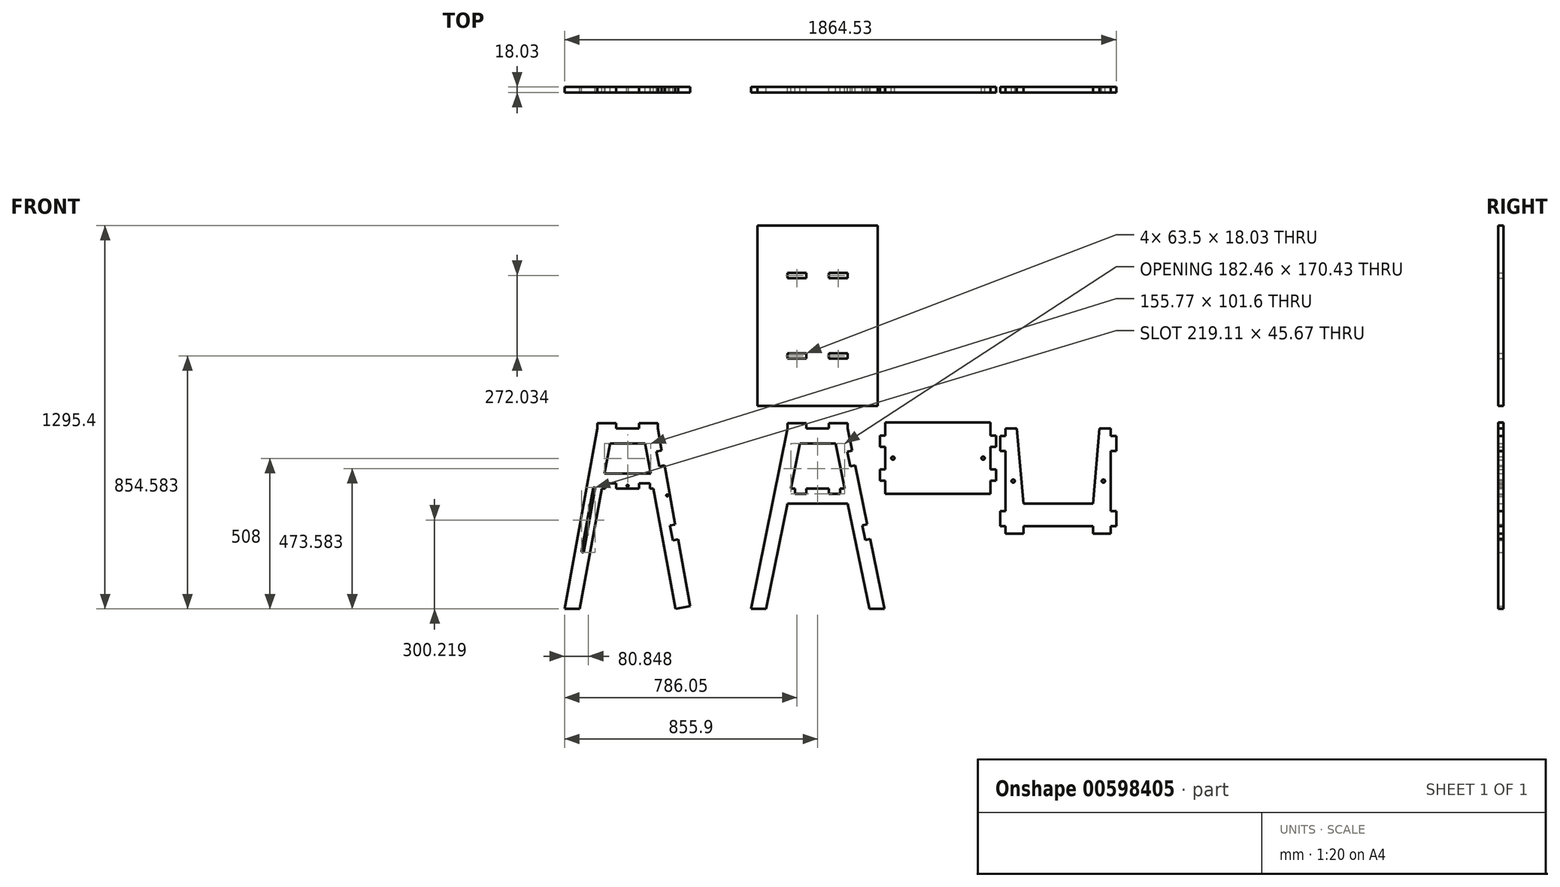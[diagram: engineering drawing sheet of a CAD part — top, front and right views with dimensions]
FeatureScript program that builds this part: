
annotation { "Feature Type Name" : "Feature", "Feature Type Description" : "" }
export const myFeature = defineFeature(function(context is Context, id is Id, definition is map)
    precondition{}
    {
        {
            var Q0;
            Q0=qCreatedBy(makeId("Front.planeOp"),FACE);
            var sketch = newSketch(context, id + "F0", { "sketchPlane" : qUnion([Q0])});
            skLineSegment(sketch, "E0", {"start": v(-101.6, 0) * mm, "end": v(101.6, 0) * mm});
            skLineSegment(sketch, "E1", {"start": v(-101.6, 0) * mm, "end": v(-226.03, -609.6) * mm});
            skLineSegment(sketch, "E2", {"start": v(-226.03, -609.6) * mm, "end": v(-174.19, -609.6) * mm});
            skLineSegment(sketch, "E3", {"start": v(-174.19, -609.6) * mm, "end": v(-101.6, -254) * mm});
            skLineSegment(sketch, "E4", {"start": v(-101.6, -254) * mm, "end": v(101.6, -254) * mm});
            skLineSegment(sketch, "E5", {"start": v(0, 0) * mm, "end": v(0, -254) * mm, "construction": true});
            skLineSegment(sketch, "E6.MirrorCS", {"start": v(226.03, -609.6) * mm, "end": v(174.19, -609.6) * mm});
            skLineSegment(sketch, "E7.MirrorCS", {"start": v(174.19, -609.6) * mm, "end": v(101.6, -254) * mm});
            skLineSegment(sketch, "E8.MirrorCS", {"start": v(101.6, 0) * mm, "end": v(226.03, -609.6) * mm});
            skLineSegment(sketch, "E9.0", {"start": v(-60.12, -50.8) * mm, "end": v(60.12, -50.8) * mm});
            skLineSegment(sketch, "E10.0", {"start": v(-91.23, -203.2) * mm, "end": v(91.23, -203.2) * mm});
            skLineSegment(sketch, "E11", {"start": v(-101.6, -254) * mm, "end": v(-60.12, -50.8) * mm, "construction": true});
            skLineSegment(sketch, "E12", {"start": v(-60.12, -50.8) * mm, "end": v(-91.23, -203.2) * mm});
            skLineSegment(sketch, "E13.MirrorCS", {"start": v(60.12, -50.8) * mm, "end": v(91.23, -203.2) * mm});
            skLineSegment(sketch, "E14", {"start": v(-101.6, 0) * mm, "end": v(-101.6, 18.03) * mm});
            skLineSegment(sketch, "E15", {"start": v(-101.6, 18.03) * mm, "end": v(-38.1, 18.03) * mm});
            skLineSegment(sketch, "E16", {"start": v(-38.1, 18.03) * mm, "end": v(-38.1, 0) * mm});
            skLineSegment(sketch, "E17", {"start": v(101.6, 0) * mm, "end": v(101.6, 18.03) * mm});
            skLineSegment(sketch, "E18", {"start": v(101.6, 18.03) * mm, "end": v(38.1, 18.03) * mm});
            skLineSegment(sketch, "E19", {"start": v(38.1, 18.03) * mm, "end": v(38.1, 0) * mm});
            skLineSegment(sketch, "E20", {"start": v(116.84, -74.66) * mm, "end": v(99.17, -78.27) * mm});
            skLineSegment(sketch, "E21", {"start": v(99.17, -78.27) * mm, "end": v(109.33, -128.04) * mm});
            skLineSegment(sketch, "E22", {"start": v(109.33, -128.04) * mm, "end": v(127, -124.43) * mm});
            skLineSegment(sketch, "E23", {"start": v(167.64, -323.53) * mm, "end": v(149.97, -327.14) * mm});
            skLineSegment(sketch, "E24", {"start": v(149.97, -327.14) * mm, "end": v(160.13, -376.9) * mm});
            skLineSegment(sketch, "E25", {"start": v(160.13, -376.9) * mm, "end": v(177.8, -373.3) * mm});
            skLineSegment(sketch, "E26.bottom", {"start": v(-76.2, -203.2) * mm, "end": v(-38.1, -203.2) * mm});
            skLineSegment(sketch, "E26.top", {"start": v(-76.2, -221.23) * mm, "end": v(-38.1, -221.23) * mm});
            skLineSegment(sketch, "E26.left", {"start": v(-76.2, -203.2) * mm, "end": v(-76.2, -221.23) * mm});
            skLineSegment(sketch, "E26.right", {"start": v(-38.1, -203.2) * mm, "end": v(-38.1, -221.23) * mm});
            skLineSegment(sketch, "E27.MirrorCS", {"start": v(76.2, -221.23) * mm, "end": v(38.1, -221.23) * mm});
            skLineSegment(sketch, "E28.MirrorCS", {"start": v(76.2, -203.2) * mm, "end": v(76.2, -221.23) * mm});
            skLineSegment(sketch, "E29.MirrorCS", {"start": v(76.2, -203.2) * mm, "end": v(38.1, -203.2) * mm});
            skLineSegment(sketch, "E30.MirrorCS", {"start": v(38.1, -203.2) * mm, "end": v(38.1, -221.23) * mm});
            skLineSegment(sketch, "E31.bottom", {"start": v(228.6, -221.23) * mm, "end": v(584.2, -221.23) * mm});
            skLineSegment(sketch, "E31.top", {"start": v(228.6, 20.07) * mm, "end": v(584.2, 20.07) * mm});
            skLineSegment(sketch, "E31.left", {"start": v(228.6, -221.23) * mm, "end": v(228.6, 20.07) * mm});
            skLineSegment(sketch, "E31.right", {"start": v(584.2, -221.23) * mm, "end": v(584.2, 20.07) * mm});
            skLineSegment(sketch, "E32", {"start": v(228.6, -100.58) * mm, "end": v(584.2, -100.58) * mm, "construction": true});
            skLineSegment(sketch, "E33.bottom", {"start": v(228.6, -62.48) * mm, "end": v(210.57, -62.48) * mm});
            skLineSegment(sketch, "E33.top", {"start": v(228.6, -24.38) * mm, "end": v(210.57, -24.38) * mm});
            skLineSegment(sketch, "E33.left", {"start": v(228.6, -62.48) * mm, "end": v(228.6, -24.38) * mm});
            skLineSegment(sketch, "E33.right", {"start": v(210.57, -62.48) * mm, "end": v(210.57, -24.38) * mm});
            skLineSegment(sketch, "E34.MirrorCS", {"start": v(210.57, -138.68) * mm, "end": v(210.57, -176.78) * mm});
            skLineSegment(sketch, "E35.MirrorCS", {"start": v(228.6, -176.78) * mm, "end": v(210.57, -176.78) * mm});
            skLineSegment(sketch, "E36.MirrorCS", {"start": v(228.6, -138.68) * mm, "end": v(228.6, -176.78) * mm});
            skLineSegment(sketch, "E37.MirrorCS", {"start": v(228.6, -138.68) * mm, "end": v(210.57, -138.68) * mm});
            skLineSegment(sketch, "E38", {"start": v(406.4, 20.07) * mm, "end": v(406.4, -221.23) * mm, "construction": true});
            skLineSegment(sketch, "E39.MirrorCS", {"start": v(602.23, -62.48) * mm, "end": v(602.23, -24.38) * mm});
            skLineSegment(sketch, "E40.MirrorCS", {"start": v(584.2, -138.68) * mm, "end": v(602.23, -138.68) * mm});
            skLineSegment(sketch, "E41.MirrorCS", {"start": v(584.2, -62.48) * mm, "end": v(584.2, -24.38) * mm});
            skLineSegment(sketch, "E42.MirrorCS", {"start": v(584.2, -176.78) * mm, "end": v(602.23, -176.78) * mm});
            skLineSegment(sketch, "E43.MirrorCS", {"start": v(584.2, -24.38) * mm, "end": v(602.23, -24.38) * mm});
            skLineSegment(sketch, "E44.MirrorCS", {"start": v(602.23, -138.68) * mm, "end": v(602.23, -176.78) * mm});
            skLineSegment(sketch, "E45.MirrorCS", {"start": v(584.2, -62.48) * mm, "end": v(602.23, -62.48) * mm});
            skLineSegment(sketch, "E46.MirrorCS", {"start": v(584.2, -138.68) * mm, "end": v(584.2, -176.78) * mm});
            skLineSegment(sketch, "E47", {"start": v(635, 0) * mm, "end": v(635, -355.6) * mm});
            skLineSegment(sketch, "E48.bottom", {"start": v(635, -25.4) * mm, "end": v(616.97, -25.4) * mm});
            skLineSegment(sketch, "E48.top", {"start": v(635, -76.2) * mm, "end": v(616.97, -76.2) * mm});
            skLineSegment(sketch, "E48.left", {"start": v(635, -25.4) * mm, "end": v(635, -76.2) * mm});
            skLineSegment(sketch, "E48.right", {"start": v(616.97, -25.4) * mm, "end": v(616.97, -76.2) * mm});
            skLineSegment(sketch, "E49.bottom", {"start": v(635, -330.2) * mm, "end": v(616.97, -330.2) * mm});
            skLineSegment(sketch, "E49.top", {"start": v(635, -279.4) * mm, "end": v(616.97, -279.4) * mm});
            skLineSegment(sketch, "E49.left", {"start": v(635, -330.2) * mm, "end": v(635, -279.4) * mm});
            skLineSegment(sketch, "E49.right", {"start": v(616.97, -330.2) * mm, "end": v(616.97, -279.4) * mm});
            skLineSegment(sketch, "E50", {"start": v(635, 0) * mm, "end": v(673.1, 0) * mm});
            skLineSegment(sketch, "E51", {"start": v(673.1, 0) * mm, "end": v(695.32, -254) * mm});
            skLineSegment(sketch, "E52", {"start": v(695.32, -254) * mm, "end": v(812.8, -254) * mm});
            skLineSegment(sketch, "E53", {"start": v(695.32, -355.6) * mm, "end": v(695.32, -330.2) * mm});
            skLineSegment(sketch, "E54", {"start": v(695.32, -330.2) * mm, "end": v(812.8, -330.2) * mm});
            skPoint(sketch, "E54.endSnap0", {"position": v(812.8, -355.6) * mm});
            skLineSegment(sketch, "E55", {"start": v(812.8, -254) * mm, "end": v(812.8, -330.2) * mm, "construction": true});
            skLineSegment(sketch, "E56.MirrorCS", {"start": v(990.6, -25.4) * mm, "end": v(1008.63, -25.4) * mm});
            skLineSegment(sketch, "E57.MirrorCS", {"start": v(990.6, -76.2) * mm, "end": v(1008.63, -76.2) * mm});
            skLineSegment(sketch, "E58.MirrorCS", {"start": v(990.6, -330.2) * mm, "end": v(1008.63, -330.2) * mm});
            skLineSegment(sketch, "E59.MirrorCS", {"start": v(990.6, -279.4) * mm, "end": v(1008.63, -279.4) * mm});
            skLineSegment(sketch, "E60.MirrorCS", {"start": v(990.6, -25.4) * mm, "end": v(990.6, -76.2) * mm});
            skLineSegment(sketch, "E61.MirrorCS", {"start": v(930.28, -355.6) * mm, "end": v(930.28, -330.2) * mm});
            skLineSegment(sketch, "E62.MirrorCS", {"start": v(990.6, -330.2) * mm, "end": v(990.6, -279.4) * mm});
            skLineSegment(sketch, "E63.MirrorCS", {"start": v(952.5, 0) * mm, "end": v(930.28, -254) * mm});
            skLineSegment(sketch, "E64.MirrorCS", {"start": v(990.6, 0) * mm, "end": v(990.6, -355.6) * mm});
            skLineSegment(sketch, "E65.MirrorCS", {"start": v(990.6, 0) * mm, "end": v(952.5, 0) * mm});
            skLineSegment(sketch, "E66.MirrorCS", {"start": v(1008.63, -25.4) * mm, "end": v(1008.63, -76.2) * mm});
            skLineSegment(sketch, "E67.MirrorCS", {"start": v(1008.63, -330.2) * mm, "end": v(1008.63, -279.4) * mm});
            skLineSegment(sketch, "E68.MirrorCS", {"start": v(930.28, -254) * mm, "end": v(812.8, -254) * mm});
            skLineSegment(sketch, "E69.MirrorCS", {"start": v(930.28, -330.2) * mm, "end": v(812.8, -330.2) * mm});
            skLineSegment(sketch, "E70", {"start": v(695.32, -355.6) * mm, "end": v(635, -355.6) * mm});
            skLineSegment(sketch, "E71", {"start": v(930.28, -355.6) * mm, "end": v(990.6, -355.6) * mm});
            skLineSegment(sketch, "E72.bottom", {"start": v(-203.2, 76.2) * mm, "end": v(203.2, 76.2) * mm});
            skLineSegment(sketch, "E72.top", {"start": v(-203.2, 685.8) * mm, "end": v(203.2, 685.8) * mm});
            skLineSegment(sketch, "E72.left", {"start": v(-203.2, 76.2) * mm, "end": v(-203.2, 685.8) * mm});
            skLineSegment(sketch, "E72.right", {"start": v(203.2, 76.2) * mm, "end": v(203.2, 685.8) * mm});
            skLineSegment(sketch, "E73", {"start": v(0, 685.8) * mm, "end": v(0, 381) * mm, "construction": true});
            skPoint(sketch, "E73.endSnap0", {"position": v(203.2, 381) * mm});
            skLineSegment(sketch, "E74", {"start": v(0, 381) * mm, "end": v(203.2, 381) * mm, "construction": true});
            skLineSegment(sketch, "E75.bottom", {"start": v(-101.6, 235.97) * mm, "end": v(-38.1, 235.97) * mm});
            skLineSegment(sketch, "E75.top", {"start": v(-101.6, 254) * mm, "end": v(-38.1, 254) * mm});
            skLineSegment(sketch, "E75.left", {"start": v(-101.6, 235.97) * mm, "end": v(-101.6, 254) * mm});
            skLineSegment(sketch, "E75.right", {"start": v(-38.1, 235.97) * mm, "end": v(-38.1, 254) * mm});
            skLineSegment(sketch, "E76.MirrorCS", {"start": v(101.6, 235.97) * mm, "end": v(38.1, 235.97) * mm});
            skLineSegment(sketch, "E77.MirrorCS", {"start": v(101.6, 254) * mm, "end": v(38.1, 254) * mm});
            skLineSegment(sketch, "E78.MirrorCS", {"start": v(38.1, 235.97) * mm, "end": v(38.1, 254) * mm});
            skLineSegment(sketch, "E79.MirrorCS", {"start": v(101.6, 235.97) * mm, "end": v(101.6, 254) * mm});
            skLineSegment(sketch, "E80.MirrorCS", {"start": v(38.1, 526.03) * mm, "end": v(38.1, 508) * mm});
            skLineSegment(sketch, "E81.MirrorCS", {"start": v(-38.1, 526.03) * mm, "end": v(-38.1, 508) * mm});
            skLineSegment(sketch, "E82.MirrorCS", {"start": v(-101.6, 526.03) * mm, "end": v(-101.6, 508) * mm});
            skLineSegment(sketch, "E83.MirrorCS", {"start": v(101.6, 526.03) * mm, "end": v(101.6, 508) * mm});
            skLineSegment(sketch, "E84.MirrorCS", {"start": v(101.6, 508) * mm, "end": v(38.1, 508) * mm});
            skLineSegment(sketch, "E85.MirrorCS", {"start": v(101.6, 526.03) * mm, "end": v(38.1, 526.03) * mm});
            skLineSegment(sketch, "E86.MirrorCS", {"start": v(-101.6, 508) * mm, "end": v(-38.1, 508) * mm});
            skLineSegment(sketch, "E87.MirrorCS", {"start": v(-101.6, 526.03) * mm, "end": v(-38.1, 526.03) * mm});
            skLineSegment(sketch, "E88", {"start": v(-744.17, 0) * mm, "end": v(-540.97, 0) * mm});
            skLineSegment(sketch, "E89", {"start": v(-744.17, 0) * mm, "end": v(-855.9, -609.6) * mm});
            skLineSegment(sketch, "E90", {"start": v(-855.9, -609.6) * mm, "end": v(-804.26, -609.6) * mm});
            skLineSegment(sketch, "E91", {"start": v(-804.26, -609.6) * mm, "end": v(-729.77, -203.2) * mm});
            skLineSegment(sketch, "E92", {"start": v(-729.77, -203.2) * mm, "end": v(-555.37, -203.2) * mm});
            skLineSegment(sketch, "E93", {"start": v(-642.57, 0) * mm, "end": v(-642.57, -203.2) * mm, "construction": true});
            skLineSegment(sketch, "E94.MirrorCS", {"start": v(-429.23, -609.6) * mm, "end": v(-480.88, -609.6) * mm});
            skLineSegment(sketch, "E95.MirrorCS", {"start": v(-480.88, -609.6) * mm, "end": v(-555.37, -203.2) * mm});
            skLineSegment(sketch, "E96.MirrorCS", {"start": v(-540.97, 0) * mm, "end": v(-429.23, -609.6) * mm});
            skLineSegment(sketch, "E97.0", {"start": v(-701.83, -50.8) * mm, "end": v(-583.3, -50.8) * mm});
            skLineSegment(sketch, "E98.0", {"start": v(-720.46, -152.4) * mm, "end": v(-564.68, -152.4) * mm});
            skLineSegment(sketch, "E99", {"start": v(-729.77, -203.2) * mm, "end": v(-701.83, -50.8) * mm, "construction": true});
            skLineSegment(sketch, "E100", {"start": v(-701.83, -50.8) * mm, "end": v(-720.46, -152.4) * mm});
            skLineSegment(sketch, "E101.MirrorCS", {"start": v(-583.3, -50.8) * mm, "end": v(-564.68, -152.4) * mm});
            skLineSegment(sketch, "E102", {"start": v(-744.17, 0) * mm, "end": v(-744.17, 18.03) * mm});
            skLineSegment(sketch, "E103", {"start": v(-744.17, 18.03) * mm, "end": v(-680.67, 18.03) * mm});
            skLineSegment(sketch, "E104", {"start": v(-680.67, 18.03) * mm, "end": v(-680.67, 0) * mm});
            skLineSegment(sketch, "E105", {"start": v(-540.97, 0) * mm, "end": v(-540.97, 18.03) * mm});
            skLineSegment(sketch, "E106", {"start": v(-540.97, 18.03) * mm, "end": v(-604.47, 18.03) * mm});
            skLineSegment(sketch, "E107", {"start": v(-604.47, 18.03) * mm, "end": v(-604.47, 0) * mm});
            skLineSegment(sketch, "E108", {"start": v(-527.23, -74.95) * mm, "end": v(-544.97, -78.2) * mm});
            skLineSegment(sketch, "E109", {"start": v(-544.97, -78.2) * mm, "end": v(-535.81, -128.17) * mm});
            skLineSegment(sketch, "E110", {"start": v(-535.81, -128.17) * mm, "end": v(-518.07, -124.92) * mm});
            skLineSegment(sketch, "E111", {"start": v(-481.44, -324.79) * mm, "end": v(-499.18, -328.04) * mm});
            skLineSegment(sketch, "E112", {"start": v(-499.18, -328.04) * mm, "end": v(-490.02, -378) * mm});
            skLineSegment(sketch, "E113", {"start": v(-490.02, -378) * mm, "end": v(-472.28, -374.76) * mm});
            skLineSegment(sketch, "E114.bottom", {"start": v(-718.77, -152.4) * mm, "end": v(-680.67, -152.4) * mm, "construction": true});
            skLineSegment(sketch, "E114.top", {"start": v(-718.77, -170.43) * mm, "end": v(-680.67, -170.43) * mm, "construction": true});
            skLineSegment(sketch, "E114.left", {"start": v(-718.77, -152.4) * mm, "end": v(-718.77, -170.43) * mm, "construction": true});
            skLineSegment(sketch, "E114.right", {"start": v(-680.67, -152.4) * mm, "end": v(-680.67, -170.43) * mm, "construction": true});
            skLineSegment(sketch, "E115.MirrorCS", {"start": v(-566.37, -170.43) * mm, "end": v(-604.47, -170.43) * mm, "construction": true});
            skLineSegment(sketch, "E116.MirrorCS", {"start": v(-566.37, -152.4) * mm, "end": v(-566.37, -170.43) * mm, "construction": true});
            skLineSegment(sketch, "E117.MirrorCS", {"start": v(-566.37, -152.4) * mm, "end": v(-604.47, -152.4) * mm, "construction": true});
            skLineSegment(sketch, "E118.MirrorCS", {"start": v(-604.47, -152.4) * mm, "end": v(-604.47, -170.43) * mm, "construction": true});
            skLineSegment(sketch, "E119.bottom", {"start": v(-718.77, -203.2) * mm, "end": v(-680.67, -203.2) * mm});
            skLineSegment(sketch, "E119.top", {"start": v(-718.77, -185.17) * mm, "end": v(-680.67, -185.17) * mm});
            skLineSegment(sketch, "E119.left", {"start": v(-718.77, -203.2) * mm, "end": v(-718.77, -185.17) * mm});
            skLineSegment(sketch, "E119.right", {"start": v(-680.67, -203.2) * mm, "end": v(-680.67, -185.17) * mm});
            skLineSegment(sketch, "E120.bottom", {"start": v(-566.37, -203.2) * mm, "end": v(-604.47, -203.2) * mm});
            skLineSegment(sketch, "E120.top", {"start": v(-566.37, -185.17) * mm, "end": v(-604.47, -185.17) * mm});
            skLineSegment(sketch, "E120.left", {"start": v(-566.37, -203.2) * mm, "end": v(-566.37, -185.17) * mm});
            skLineSegment(sketch, "E120.right", {"start": v(-604.47, -203.2) * mm, "end": v(-604.47, -185.17) * mm});
            skCircle(sketch, "E121", {"center": v(-642.57, -194.18) * mm, "radius": 3.3 * mm});
            skPoint(sketch, "E121.centerSnap0", {"position": v(-680.67, -194.18) * mm});
            skLineSegment(sketch, "E122", {"start": v(-526.94, -126.54) * mm, "end": v(-490.3, -326.41) * mm, "construction": true});
            skLineSegment(sketch, "E123", {"start": v(625.98, -76.2) * mm, "end": v(625.98, -279.4) * mm, "construction": true});
            skCircle(sketch, "E124", {"center": v(660.4, -177.8) * mm, "radius": 5.59 * mm});
            skPoint(sketch, "E124.centerSnap0", {"position": v(635, -177.8) * mm});
            skCircle(sketch, "E125", {"center": v(254, -100.58) * mm, "radius": 5.59 * mm});
            skCircle(sketch, "E126", {"center": v(-508.62, -226.48) * mm, "radius": 3.3 * mm});
            skLineSegment(sketch, "E127", {"start": v(-480.88, -609.6) * mm, "end": v(-430.91, -600.44) * mm});
            skLineSegment(sketch, "E128", {"start": v(-804.26, -609.6) * mm, "end": v(-854.22, -600.44) * mm});
            skCircle(sketch, "E129.MirrorC", {"center": v(558.8, -100.58) * mm, "radius": 5.59 * mm});
            skCircle(sketch, "E130.MirrorC", {"center": v(965.2, -177.8) * mm, "radius": 5.59 * mm});
            skLineSegment(sketch, "E131", {"start": v(-829.24, -605.02) * mm, "end": v(-755.59, -203.2) * mm, "construction": true});
            skLineSegment(sketch, "E132", {"start": v(-755.59, -203.2) * mm, "end": v(-794.51, -415.56) * mm});
            skArc(sketch, "E133.0.startCap", {"start": v(-758.96, -202.58) * mm, "mid": v(-754.97, -199.83) * mm, "end": v(-752.22, -203.82) * mm});
            skArc(sketch, "E133.0.endCap", {"start": v(-791.14, -416.18) * mm, "mid": v(-795.13, -418.94) * mm, "end": v(-797.89, -414.94) * mm});
            skLineSegment(sketch, "E133.0.left", {"start": v(-752.22, -203.82) * mm, "end": v(-791.14, -416.18) * mm});
            skLineSegment(sketch, "E133.0.right", {"start": v(-758.96, -202.58) * mm, "end": v(-797.89, -414.94) * mm});
            skSolve(sketch);
        }
        {
            var Q0;
            Q0=makeQuery(id+"F0.imprint","IMPRINT",FACE,{"disambiguationData":[TD([[makeQuery(id+"F0.imprint","IMPRINT",EDGE,{"derivedFrom":sQuery(id+"F0.wireOp",EDGE,"E72.bottom")}),1.0]])]});
            var Q1;
            {var subQ13=sQuery(id+"F0.wireOp",EDGE,"E1");Q1=makeQuery(id+"F0.imprint","IMPRINT",FACE,{"disambiguationData":[TD([[makeQuery(id+"F0.imprint","IMPRINT",EDGE,{"derivedFrom":subQ13}),1.0]])]});}
            var Q2;
            {var subQ0=sQuery(id+"F0.wireOp",EDGE,"E17");Q2=makeQuery(id+"F0.imprint","IMPRINT",FACE,{"disambiguationData":[TD([[makeQuery(id+"F0.imprint","IMPRINT",EDGE,{"derivedFrom":subQ0}),1.0]])]});}
            var Q3;
            {var subQ2=sQuery(id+"F0.wireOp",EDGE,"E14");Q3=makeQuery(id+"F0.imprint","IMPRINT",FACE,{"disambiguationData":[TD([[makeQuery(id+"F0.imprint","IMPRINT",EDGE,{"derivedFrom":subQ2}),-1.0]])]});}
            var Q4;
            {var subQ1=sQuery(id+"F0.wireOp",EDGE,"E31.bottom");Q4=makeQuery(id+"F0.imprint","IMPRINT",FACE,{"disambiguationData":[TD([[makeQuery(id+"F0.imprint","IMPRINT",EDGE,{"derivedFrom":subQ1}),1.0]])]});}
            var Q5;
            {var subQ0=sQuery(id+"F0.wireOp",EDGE,"E33.bottom");Q5=makeQuery(id+"F0.imprint","IMPRINT",FACE,{"disambiguationData":[TD([[makeQuery(id+"F0.imprint","IMPRINT",EDGE,{"derivedFrom":subQ0}),-1.0]])]});}
            var Q6;
            Q6=makeQuery(id+"F0.imprint","IMPRINT",FACE,{"disambiguationData":[TD([[makeQuery(id+"F0.imprint","IMPRINT",EDGE,{"derivedFrom":sQuery(id+"F0.wireOp",EDGE,"E34.MirrorCS")}),1.0]])]});
            var Q7;
            {var subQ0=sQuery(id+"F0.wireOp",EDGE,"E40.MirrorCS");Q7=makeQuery(id+"F0.imprint","IMPRINT",FACE,{"disambiguationData":[TD([[makeQuery(id+"F0.imprint","IMPRINT",EDGE,{"derivedFrom":subQ0}),-1.0]])]});}
            var Q8;
            Q8=makeQuery(id+"F0.imprint","IMPRINT",FACE,{"disambiguationData":[TD([[makeQuery(id+"F0.imprint","IMPRINT",EDGE,{"derivedFrom":sQuery(id+"F0.wireOp",EDGE,"E39.MirrorCS")}),1.0]])]});
            var Q9;
            {var subQ8=sQuery(id+"F0.wireOp",EDGE,"E50");Q9=makeQuery(id+"F0.imprint","IMPRINT",FACE,{"disambiguationData":[TD([[makeQuery(id+"F0.imprint","IMPRINT",EDGE,{"derivedFrom":subQ8}),-1.0]])]});}
            var Q10;
            Q10=makeQuery(id+"F0.imprint","IMPRINT",FACE,{"disambiguationData":[TD([[makeQuery(id+"F0.imprint","IMPRINT",EDGE,{"derivedFrom":sQuery(id+"F0.wireOp",EDGE,"E56.MirrorCS")}),-1.0]])]});
            var Q11;
            {var subQ2=sQuery(id+"F0.wireOp",EDGE,"E48.bottom");Q11=makeQuery(id+"F0.imprint","IMPRINT",FACE,{"disambiguationData":[TD([[makeQuery(id+"F0.imprint","IMPRINT",EDGE,{"derivedFrom":subQ2}),1.0]])]});}
            var Q12;
            {var subQ0=sQuery(id+"F0.wireOp",EDGE,"E49.bottom");Q12=makeQuery(id+"F0.imprint","IMPRINT",FACE,{"disambiguationData":[TD([[makeQuery(id+"F0.imprint","IMPRINT",EDGE,{"derivedFrom":subQ0}),-1.0]])]});}
            var Q13;
            Q13=makeQuery(id+"F0.imprint","IMPRINT",FACE,{"disambiguationData":[TD([[makeQuery(id+"F0.imprint","IMPRINT",EDGE,{"derivedFrom":sQuery(id+"F0.wireOp",EDGE,"E58.MirrorCS")}),1.0]])]});
            var Q14;
            {var subQ0=sQuery(id+"F0.wireOp",EDGE,"E90");Q14=makeQuery(id+"F0.imprint","IMPRINT",FACE,{"disambiguationData":[TD([[makeQuery(id+"F0.imprint","IMPRINT",EDGE,{"derivedFrom":subQ0}),1.0]])]});}
            var Q15;
            {var subQ0=sQuery(id+"F0.wireOp",EDGE,"E105");Q15=makeQuery(id+"F0.imprint","IMPRINT",FACE,{"disambiguationData":[TD([[makeQuery(id+"F0.imprint","IMPRINT",EDGE,{"derivedFrom":subQ0}),1.0]])]});}
            var Q16;
            {var subQ2=sQuery(id+"F0.wireOp",EDGE,"E102");Q16=makeQuery(id+"F0.imprint","IMPRINT",FACE,{"disambiguationData":[TD([[makeQuery(id+"F0.imprint","IMPRINT",EDGE,{"derivedFrom":subQ2}),-1.0]])]});}
            var Q17;
            {var subQ15=sQuery(id+"F0.wireOp",EDGE,"E91");Q17=makeQuery(id+"F0.imprint","IMPRINT",FACE,{"disambiguationData":[TD([[makeQuery(id+"F0.imprint","IMPRINT",EDGE,{"derivedFrom":subQ15}),1.0]])]});}
            extrude(context, id + "F1", {"entities" : qUnion([Q0, Q1, Q2, Q3, Q4, Q5, Q6, Q7, Q8, Q9, Q10, Q11, Q12, Q13, Q14, Q15, Q16, Q17]), "depth" : 18.03 * mm, "offsetDistance" : 25.4 * mm});
        }
    });
